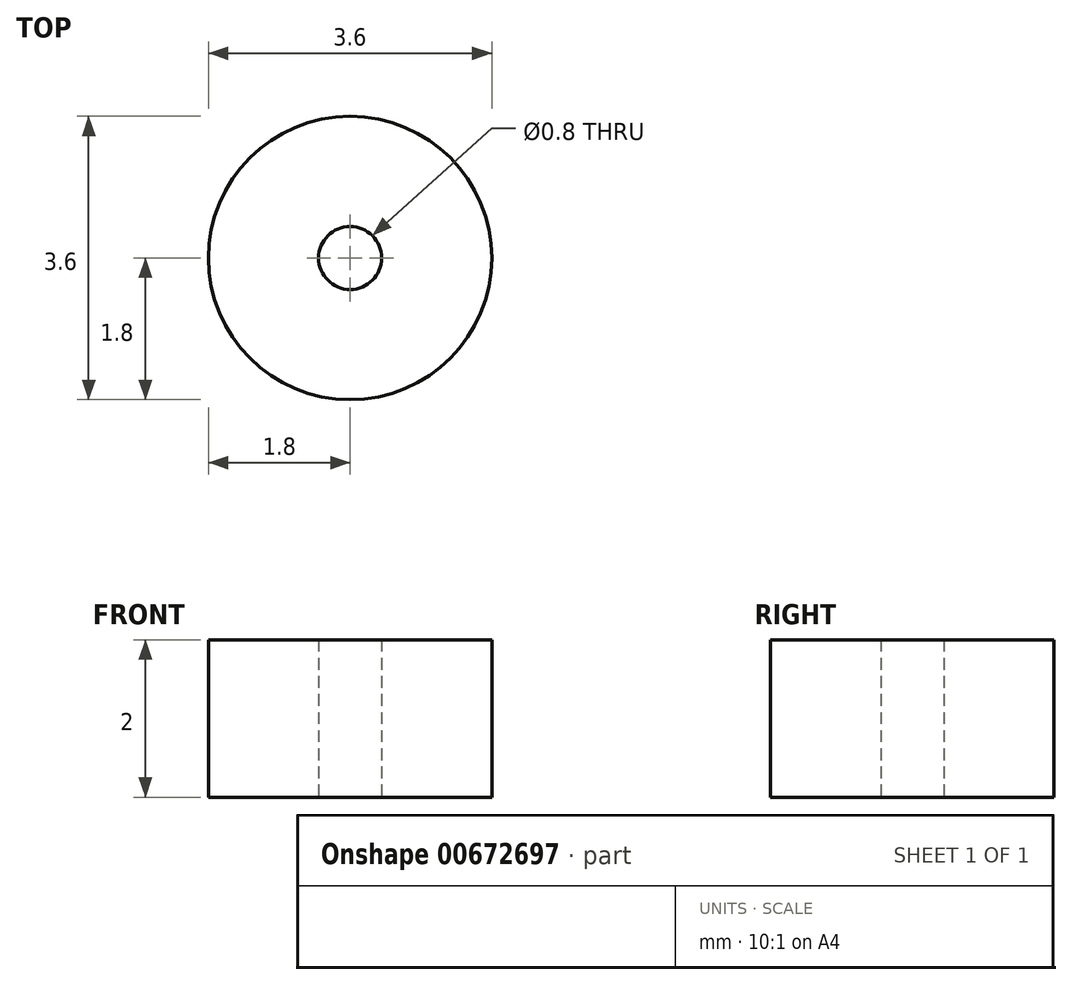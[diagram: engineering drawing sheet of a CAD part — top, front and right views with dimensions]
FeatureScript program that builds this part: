
annotation { "Feature Type Name" : "Feature", "Feature Type Description" : "" }
export const myFeature = defineFeature(function(context is Context, id is Id, definition is map)
    precondition{}
    {
        {
            var Q0;
            Q0=qCreatedBy(makeId("Top.planeOp"),FACE);
            var sketch = newSketch(context, id + "F0", { "sketchPlane" : qUnion([Q0])});
            skCircle(sketch, "E0", {"center": v(0, 0) * mm, "radius": 0.4 * mm});
            skCircle(sketch, "E1", {"center": v(0, 0) * mm, "radius": 1.8 * mm});
            skSolve(sketch);
        }
        {
            var Q0;
            Q0=makeQuery(id+"F0.imprint","IMPRINT",FACE,{"disambiguationData":[TD([[makeQuery(id+"F0.imprint","IMPRINT",EDGE,{"derivedFrom":sQuery(id+"F0.wireOp",EDGE,"E0")}),-1.0]])]});
            extrude(context, id + "F1", {"entities" : qUnion([Q0]), "depth" : 2 * mm, "offsetDistance" : 25 * mm});
        }
    });
